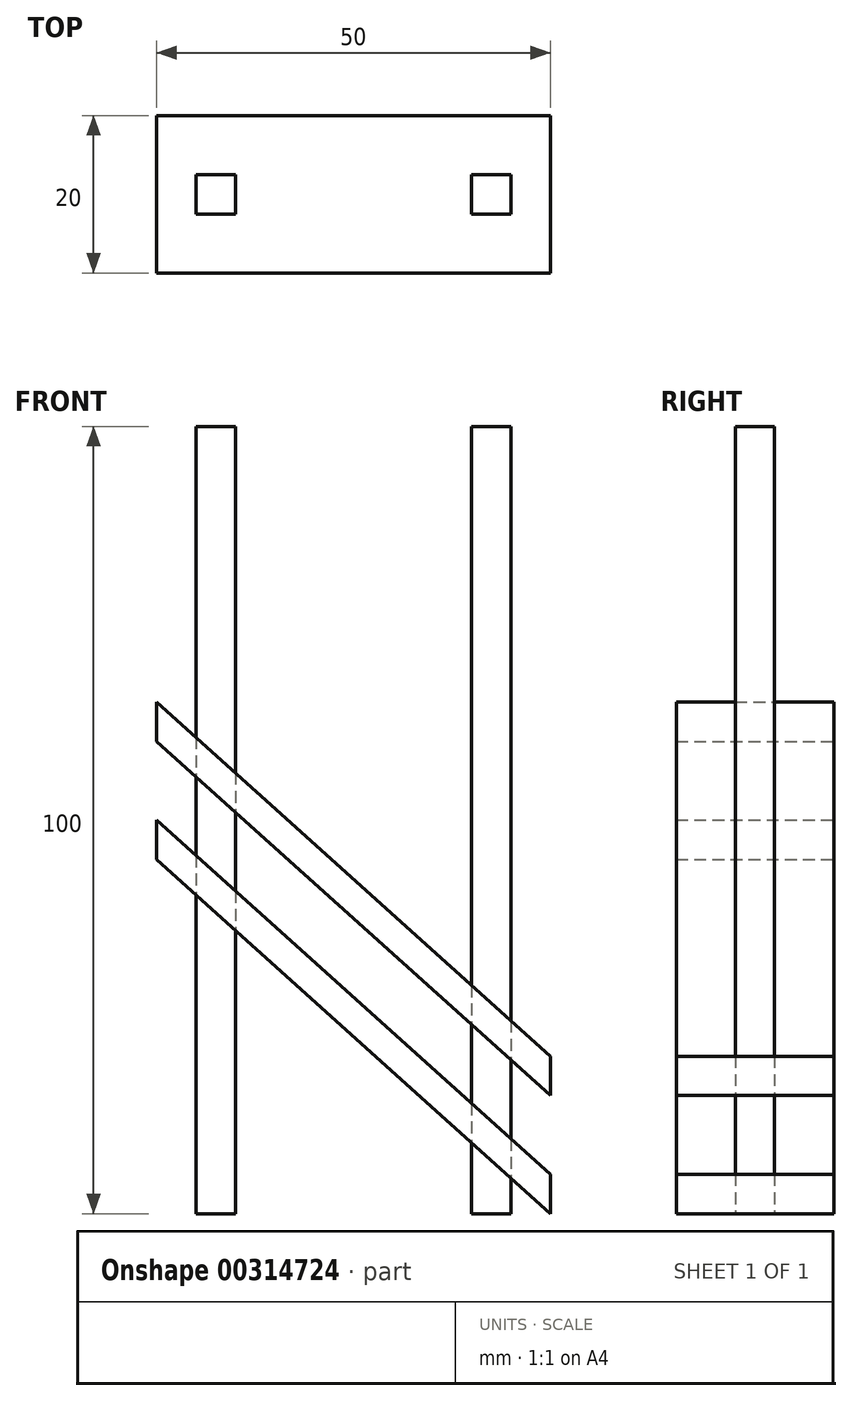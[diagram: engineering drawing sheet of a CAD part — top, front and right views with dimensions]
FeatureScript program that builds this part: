
annotation { "Feature Type Name" : "Feature", "Feature Type Description" : "" }
export const myFeature = defineFeature(function(context is Context, id is Id, definition is map)
    precondition{}
    {
        {
            var Q0;
            Q0=qCreatedBy(makeId("Front.planeOp"),FACE);
            var sketch = newSketch(context, id + "F0", { "sketchPlane" : qUnion([Q0])});
            skLineSegment(sketch, "E0.bottom", {"start": v(-52.93, 55) * mm, "end": v(-47.93, 55) * mm});
            skLineSegment(sketch, "E0.top", {"start": v(-52.93, -45) * mm, "end": v(-47.93, -45) * mm});
            skLineSegment(sketch, "E0.left", {"start": v(-52.93, 55) * mm, "end": v(-52.93, -45) * mm});
            skLineSegment(sketch, "E0.right", {"start": v(-47.93, 55) * mm, "end": v(-47.93, -45) * mm});
            skLineSegment(sketch, "E1.MirrorCS", {"start": v(-12.93, 55) * mm, "end": v(-17.93, 55) * mm});
            skLineSegment(sketch, "E2.MirrorCS", {"start": v(-12.93, -45) * mm, "end": v(-17.93, -45) * mm});
            skLineSegment(sketch, "E3.MirrorCS", {"start": v(-12.93, 55) * mm, "end": v(-12.93, -45) * mm});
            skLineSegment(sketch, "E4.MirrorCS", {"start": v(-17.93, 55) * mm, "end": v(-17.93, -45) * mm});
            skPoint(sketch, "E5", {"position": v(-47.93, 5) * mm});
            skPoint(sketch, "E6", {"position": v(-17.93, 5) * mm});
            skPoint(sketch, "E7", {"position": v(-12.93, 5) * mm});
            skPoint(sketch, "E8", {"position": v(-52.93, 5) * mm});
            skLineSegment(sketch, "E9", {"start": v(-57.93, 5) * mm, "end": v(-57.93, 0) * mm});
            skLineSegment(sketch, "E10", {"start": v(-57.93, 0) * mm, "end": v(-7.93, -45) * mm});
            skLineSegment(sketch, "E11", {"start": v(-7.93, -45) * mm, "end": v(-7.93, -40) * mm});
            skLineSegment(sketch, "E12", {"start": v(-7.93, -40) * mm, "end": v(-57.93, 5) * mm});
            skPoint(sketch, "E13", {"position": v(-12.93, -45) * mm});
            skLineSegment(sketch, "E14", {"start": v(-57.93, 20) * mm, "end": v(-57.93, 15) * mm});
            skLineSegment(sketch, "E15", {"start": v(-57.93, 15) * mm, "end": v(-7.93, -30) * mm});
            skLineSegment(sketch, "E16", {"start": v(-7.93, -30) * mm, "end": v(-7.93, -25) * mm});
            skLineSegment(sketch, "E17", {"start": v(-7.93, -25) * mm, "end": v(-57.93, 20) * mm});
            skSolve(sketch);
        }
        {
            var Q0;
            {var subQ0=sQuery(id+"F0.wireOp",EDGE,"E0.bottom");Q0=makeQuery(id+"F0.imprint","IMPRINT",FACE,{"disambiguationData":[TD([[makeQuery(id+"F0.imprint","IMPRINT",EDGE,{"derivedFrom":subQ0}),-1.0]])]});}
            var Q1;
            {var subQ0=sQuery(id+"F0.wireOp",EDGE,"E0.top");Q1=makeQuery(id+"F0.imprint","IMPRINT",FACE,{"disambiguationData":[TD([[makeQuery(id+"F0.imprint","IMPRINT",EDGE,{"derivedFrom":subQ0}),1.0]])]});}
            var Q2;
            {var subQ0=sQuery(id+"F0.wireOp",EDGE,"E1.MirrorCS");Q2=makeQuery(id+"F0.imprint","IMPRINT",FACE,{"disambiguationData":[TD([[makeQuery(id+"F0.imprint","IMPRINT",EDGE,{"derivedFrom":subQ0}),1.0]])]});}
            var Q3;
            {var subQ0=sQuery(id+"F0.wireOp",EDGE,"E2.MirrorCS");Q3=makeQuery(id+"F0.imprint","IMPRINT",FACE,{"disambiguationData":[TD([[makeQuery(id+"F0.imprint","IMPRINT",EDGE,{"derivedFrom":subQ0}),-1.0]])]});}
            var Q4;
            {var subQ0=sQuery(id+"F0.wireOp",EDGE,"E15");var subQ1=sQuery(id+"F0.wireOp",EDGE,"E0.left");var subQ2=makeQuery(id+"F0.imprint","INTERSECT",VERTEX,{"derivedFrom":[subQ1,subQ0]});Q4=makeQuery(id+"F0.imprint","IMPRINT",FACE,{"disambiguationData":[TD([[makeQuery(id+"F0.imprint","IMPRINT",EDGE,{"disambiguationData":[TD([[subQ2,-1.0]])],"derivedFrom":subQ1}),1.0]])]});}
            var Q5;
            {var subQ0=sQuery(id+"F0.wireOp",EDGE,"E15");var subQ1=sQuery(id+"F0.wireOp",EDGE,"E3.MirrorCS");var subQ2=makeQuery(id+"F0.imprint","INTERSECT",VERTEX,{"derivedFrom":[subQ1,subQ0]});Q5=makeQuery(id+"F0.imprint","IMPRINT",FACE,{"disambiguationData":[TD([[makeQuery(id+"F0.imprint","IMPRINT",EDGE,{"disambiguationData":[TD([[subQ2,-1.0]])],"derivedFrom":subQ1}),-1.0]])]});}
            var Q6;
            {var subQ0=sQuery(id+"F0.wireOp",EDGE,"E17");var subQ1=sQuery(id+"F0.wireOp",EDGE,"E0.left");var subQ2=makeQuery(id+"F0.imprint","INTERSECT",VERTEX,{"derivedFrom":[subQ1,subQ0]});Q6=makeQuery(id+"F0.imprint","IMPRINT",FACE,{"disambiguationData":[TD([[makeQuery(id+"F0.imprint","IMPRINT",EDGE,{"disambiguationData":[TD([[subQ2,-1.0]])],"derivedFrom":subQ1}),1.0]])]});}
            var Q7;
            {var subQ0=sQuery(id+"F0.wireOp",EDGE,"E12");var subQ1=sQuery(id+"F0.wireOp",EDGE,"E0.left");var subQ2=makeQuery(id+"F0.imprint","INTERSECT",VERTEX,{"derivedFrom":[subQ1,subQ0]});Q7=makeQuery(id+"F0.imprint","IMPRINT",FACE,{"disambiguationData":[TD([[makeQuery(id+"F0.imprint","IMPRINT",EDGE,{"disambiguationData":[TD([[subQ2,-1.0]])],"derivedFrom":subQ1}),1.0]])]});}
            var Q8;
            {var subQ0=sQuery(id+"F0.wireOp",EDGE,"E17");var subQ1=sQuery(id+"F0.wireOp",EDGE,"E3.MirrorCS");var subQ2=makeQuery(id+"F0.imprint","INTERSECT",VERTEX,{"derivedFrom":[subQ1,subQ0]});Q8=makeQuery(id+"F0.imprint","IMPRINT",FACE,{"disambiguationData":[TD([[makeQuery(id+"F0.imprint","IMPRINT",EDGE,{"disambiguationData":[TD([[subQ2,-1.0]])],"derivedFrom":subQ1}),-1.0]])]});}
            var Q9;
            {var subQ0=sQuery(id+"F0.wireOp",EDGE,"E12");var subQ1=sQuery(id+"F0.wireOp",EDGE,"E3.MirrorCS");var subQ2=makeQuery(id+"F0.imprint","INTERSECT",VERTEX,{"derivedFrom":[subQ1,subQ0]});Q9=makeQuery(id+"F0.imprint","IMPRINT",FACE,{"disambiguationData":[TD([[makeQuery(id+"F0.imprint","IMPRINT",EDGE,{"disambiguationData":[TD([[subQ2,-1.0]])],"derivedFrom":subQ1}),-1.0]])]});}
            extrude(context, id + "F1", {"entities" : qUnion([Q0, Q1, Q2, Q3, Q4, Q5, Q6, Q7, Q8, Q9]), "depth" : 2.5 * mm, "hasSecondDirection" : true, "secondDirectionOppositeDirection" : true, "secondDirectionDepth" : 2.5 * mm});
        }
        {
            var Q0;
            {var subQ0=sQuery(id+"F0.wireOp",EDGE,"E17");var subQ1=sQuery(id+"F0.wireOp",EDGE,"E0.right");var subQ2=makeQuery(id+"F0.imprint","INTERSECT",VERTEX,{"derivedFrom":[subQ1,subQ0]});Q0=makeQuery(id+"F0.imprint","IMPRINT",FACE,{"disambiguationData":[TD([[makeQuery(id+"F0.imprint","IMPRINT",EDGE,{"disambiguationData":[TD([[subQ2,-1.0]])],"derivedFrom":subQ1}),1.0]])]});}
            var Q1;
            {var subQ0=sQuery(id+"F0.wireOp",EDGE,"E10");var subQ1=sQuery(id+"F0.wireOp",EDGE,"E0.right");var subQ2=makeQuery(id+"F0.imprint","INTERSECT",VERTEX,{"derivedFrom":[subQ1,subQ0]});Q1=makeQuery(id+"F0.imprint","IMPRINT",FACE,{"disambiguationData":[TD([[makeQuery(id+"F0.imprint","IMPRINT",EDGE,{"disambiguationData":[TD([[subQ2,1.0]])],"derivedFrom":subQ1}),1.0]])]});}
            var Q2;
            {var subQ5=sQuery(id+"F0.wireOp",EDGE,"E9");Q2=makeQuery(id+"F0.imprint","IMPRINT",FACE,{"disambiguationData":[TD([[makeQuery(id+"F0.imprint","IMPRINT",EDGE,{"derivedFrom":subQ5}),1.0]])]});}
            var Q3;
            {var subQ5=sQuery(id+"F0.wireOp",EDGE,"E14");Q3=makeQuery(id+"F0.imprint","IMPRINT",FACE,{"disambiguationData":[TD([[makeQuery(id+"F0.imprint","IMPRINT",EDGE,{"derivedFrom":subQ5}),1.0]])]});}
            var Q4;
            {var subQ5=sQuery(id+"F0.wireOp",EDGE,"E16");Q4=makeQuery(id+"F0.imprint","IMPRINT",FACE,{"disambiguationData":[TD([[makeQuery(id+"F0.imprint","IMPRINT",EDGE,{"derivedFrom":subQ5}),1.0]])]});}
            var Q5;
            {var subQ5=sQuery(id+"F0.wireOp",EDGE,"E11");Q5=makeQuery(id+"F0.imprint","IMPRINT",FACE,{"disambiguationData":[TD([[makeQuery(id+"F0.imprint","IMPRINT",EDGE,{"derivedFrom":subQ5}),1.0]])]});}
            var Q6;
            {var subQ0=sQuery(id+"F0.wireOp",EDGE,"E12");var subQ1=sQuery(id+"F0.wireOp",EDGE,"E0.left");var subQ2=makeQuery(id+"F0.imprint","INTERSECT",VERTEX,{"derivedFrom":[subQ1,subQ0]});Q6=makeQuery(id+"F0.imprint","IMPRINT",FACE,{"disambiguationData":[TD([[makeQuery(id+"F0.imprint","IMPRINT",EDGE,{"disambiguationData":[TD([[subQ2,-1.0]])],"derivedFrom":subQ1}),1.0]])]});}
            var Q7;
            {var subQ0=sQuery(id+"F0.wireOp",EDGE,"E17");var subQ1=sQuery(id+"F0.wireOp",EDGE,"E0.left");var subQ2=makeQuery(id+"F0.imprint","INTERSECT",VERTEX,{"derivedFrom":[subQ1,subQ0]});Q7=makeQuery(id+"F0.imprint","IMPRINT",FACE,{"disambiguationData":[TD([[makeQuery(id+"F0.imprint","IMPRINT",EDGE,{"disambiguationData":[TD([[subQ2,-1.0]])],"derivedFrom":subQ1}),1.0]])]});}
            var Q8;
            {var subQ0=sQuery(id+"F0.wireOp",EDGE,"E17");var subQ1=sQuery(id+"F0.wireOp",EDGE,"E3.MirrorCS");var subQ2=makeQuery(id+"F0.imprint","INTERSECT",VERTEX,{"derivedFrom":[subQ1,subQ0]});Q8=makeQuery(id+"F0.imprint","IMPRINT",FACE,{"disambiguationData":[TD([[makeQuery(id+"F0.imprint","IMPRINT",EDGE,{"disambiguationData":[TD([[subQ2,-1.0]])],"derivedFrom":subQ1}),-1.0]])]});}
            var Q9;
            {var subQ0=sQuery(id+"F0.wireOp",EDGE,"E12");var subQ1=sQuery(id+"F0.wireOp",EDGE,"E3.MirrorCS");var subQ2=makeQuery(id+"F0.imprint","INTERSECT",VERTEX,{"derivedFrom":[subQ1,subQ0]});Q9=makeQuery(id+"F0.imprint","IMPRINT",FACE,{"disambiguationData":[TD([[makeQuery(id+"F0.imprint","IMPRINT",EDGE,{"disambiguationData":[TD([[subQ2,-1.0]])],"derivedFrom":subQ1}),-1.0]])]});}
            extrude(context, id + "F2", {"entities" : qUnion([Q0, Q1, Q2, Q3, Q4, Q5, Q6, Q7, Q8, Q9]), "depth" : 10 * mm, "hasSecondDirection" : true, "secondDirectionOppositeDirection" : true, "secondDirectionDepth" : 10 * mm});
        }
    });
